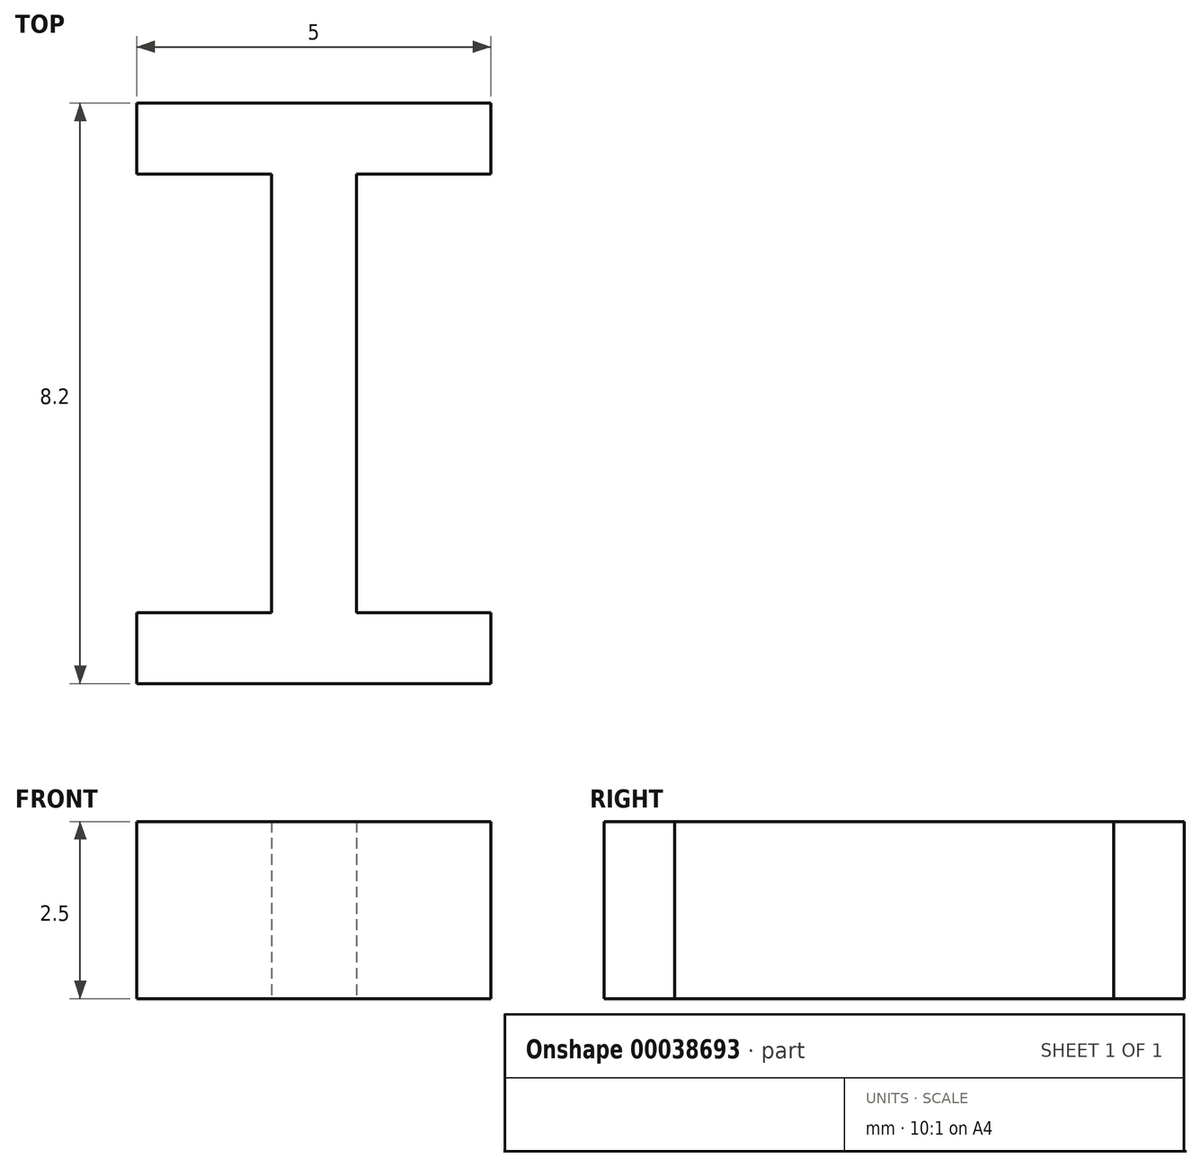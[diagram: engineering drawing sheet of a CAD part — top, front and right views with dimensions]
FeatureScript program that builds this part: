
annotation { "Feature Type Name" : "Feature", "Feature Type Description" : "" }
export const myFeature = defineFeature(function(context is Context, id is Id, definition is map)
    precondition{}
    {
        {
            var Q0;
            Q0=qCreatedBy(makeId("Top.planeOp"),FACE);
            var sketch = newSketch(context, id + "F0", { "sketchPlane" : qUnion([Q0])});
            skLineSegment(sketch, "E0.rect.bottom", {"start": v(0.6, -3.1) * mm, "end": v(-0.6, -3.1) * mm});
            skLineSegment(sketch, "E0.rect.top", {"start": v(0.6, 3.1) * mm, "end": v(-0.6, 3.1) * mm});
            skLineSegment(sketch, "E0.rect.left", {"start": v(0.6, -3.1) * mm, "end": v(0.6, 3.1) * mm});
            skLineSegment(sketch, "E0.rect.right", {"start": v(-0.6, -3.1) * mm, "end": v(-0.6, 3.1) * mm});
            skPoint(sketch, "E0.rect.middle", {"position": v(0, 0) * mm});
            skLineSegment(sketch, "E1.bottom", {"start": v(-2.5, -3.1) * mm, "end": v(2.5, -3.1) * mm});
            skLineSegment(sketch, "E1.top", {"start": v(-2.5, -4.1) * mm, "end": v(2.5, -4.1) * mm});
            skLineSegment(sketch, "E1.left", {"start": v(-2.5, -3.1) * mm, "end": v(-2.5, -4.1) * mm});
            skLineSegment(sketch, "E1.right", {"start": v(2.5, -3.1) * mm, "end": v(2.5, -4.1) * mm});
            skLineSegment(sketch, "E2.bottom", {"start": v(-2.5, 3.1) * mm, "end": v(2.5, 3.1) * mm});
            skLineSegment(sketch, "E2.top", {"start": v(-2.5, 4.1) * mm, "end": v(2.5, 4.1) * mm});
            skLineSegment(sketch, "E2.left", {"start": v(-2.5, 3.1) * mm, "end": v(-2.5, 4.1) * mm});
            skLineSegment(sketch, "E2.right", {"start": v(2.5, 3.1) * mm, "end": v(2.5, 4.1) * mm});
            skLineSegment(sketch, "E3", {"start": v(0, 4.1) * mm, "end": v(0, -4.1) * mm, "construction": true});
            skSolve(sketch);
        }
        {
            var Q0;
            Q0 = qSketchRegion(id + "F0", true);
            extrude(context, id + "F1", {"entities" : qUnion([Q0]), "depth" : 2.5 * mm});
        }
    });
